FCSTD DOCUMENT  (FreeCAD 1.1R14555 (Git shallow))
Label: Well
License: All rights reserved
LicenseURL: https://en.wikipedia.org/wiki/All_rights_reserved
objects: App::Point×1, Sketcher::SketchObject×1, PartDesign::Body×1
note: 3 computed .brp shape members not serialized (recipe doc carries the construction recipe); baked Part::Feature solids carry a one-line shape summary decoded from their .brp

FEATURE [App::Point] Origin001
  Role = Origin
FEATURE [Sketcher::SketchObject] Sketch
  ArcFitTolerance = 1e-06
  AttachmentSupport = -> [Origin]
  ExternalTypes = [0]
  FullyConstrained = false
  MakeInternals = false
  MapMode = 5
  sketch-geometry (15):
    g0: LineSegment StartX=-55 StartY=0 StartZ=0 EndX=-55 EndY=-8500 EndZ=0
    g1: LineSegment StartX=-55 StartY=-8500 StartZ=0 EndX=55 EndY=-8500 EndZ=0
    g2: LineSegment StartX=55 StartY=-8500 StartZ=0 EndX=55 EndY=0 EndZ=0
    g3: LineSegment StartX=55 StartY=0 StartZ=0 EndX=-55 EndY=0 EndZ=0
    g4: GeomPoint [constr] X=8.3e-15 Y=-4250 Z=0
    g5: GeomPoint X=0 Y=0 Z=0
    g6: LineSegment StartX=-55 StartY=-3900 StartZ=0 EndX=55 EndY=-3900 EndZ=0
    g7: LineSegment [constr] StartX=-397.581 StartY=-6400 StartZ=0 EndX=-301.581 EndY=-6400 EndZ=0
    g8: LineSegment [constr] StartX=-301.581 StartY=-6400 StartZ=0 EndX=-301.581 EndY=-5800 EndZ=0
    g9: LineSegment [constr] StartX=-301.581 StartY=-5800 StartZ=0 EndX=-397.581 EndY=-5800 EndZ=0
    g10: LineSegment [constr] StartX=-397.581 StartY=-5800 StartZ=0 EndX=-397.581 EndY=-6400 EndZ=0
    g11: GeomPoint [constr] X=-349.581 Y=-6100 Z=0
    g12: LineSegment [constr] StartX=-496.1 StartY=-3900 StartZ=0 EndX=-496.099 EndY=-6400 EndZ=0
    g13: LineSegment [constr] StartX=-349.581 StartY=-6400 StartZ=0 EndX=-349.581 EndY=-7000 EndZ=0
    g14: LineSegment StartX=-397.581 StartY=-6400 StartZ=0 EndX=-397.581 EndY=-8500 EndZ=0
  constraints (38):
    c: Coincident(g0,g1)
    c: Coincident(g1,g2)
    c: Coincident(g2,g3)
    c: Coincident(g3,g0)
    c: Vertical(g0)
    c: Vertical(g2)
    c: Horizontal(g1)
    c: Horizontal(g3)
    c: Symmetric(g2,g0,g4)
    c: Symmetric(g0,g2,g5)
    c: Coincident(g5,g-1)
    c: Distance(g3,g3) = 110
    c: DistanceY(g2,g2) = 8500
    c: Horizontal(g6)
    c: PointOnObject(g6,g2)
    c: PointOnObject(g6,g0)
    c: DistanceY(g6,g0) = 3900
    c: Coincident(g7,g8)
    c: Coincident(g8,g9)
    c: Coincident(g9,g10)
    c: Coincident(g10,g7)
    c: Horizontal(g7)
    c: Horizontal(g9)
    c: Vertical(g8)
    c: Vertical(g10)
    c: Symmetric(g9,g7,g11)
    c: Distance(g8,g10) = 96
    c: Distance(g7,g9) = 600
    c: Distance(g12) = 2500
    c: Angle(g-1,g12) = -1.5708
    c: Horizontal(g12,g6)
    c: Horizontal(g12,g7)
    c: Distance(g13) = 600
    c: Angle(g-1,g13) = -1.5708
    c: Symmetric(g7,g7,g13)
    c: Vertical(g14)
    c: Coincident(g14,g7)
    c: Horizontal(g14,g0)
FEATURE [PartDesign::Body] Body
  AllowCompound = false
  Group = -> [Sketch]
  Origin = -> Origin
